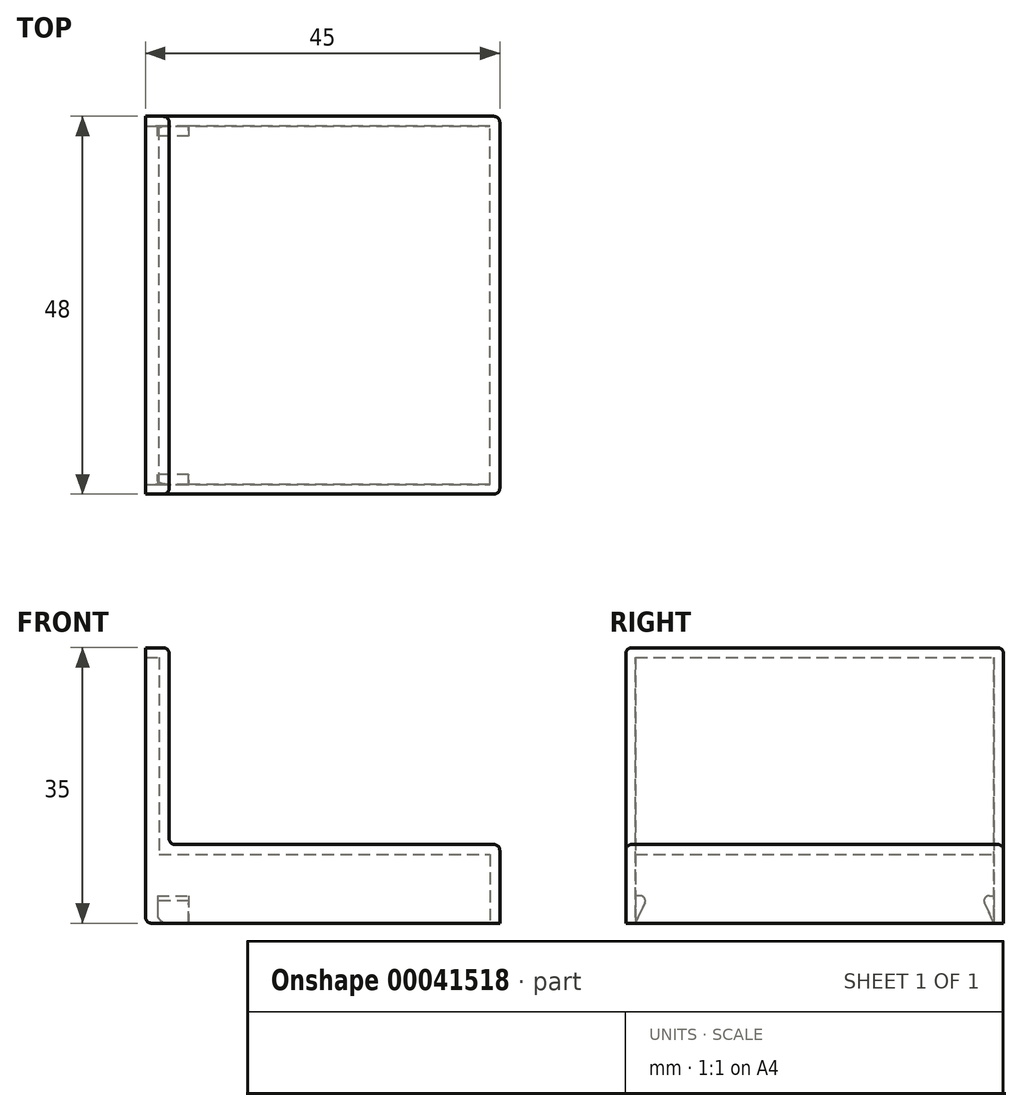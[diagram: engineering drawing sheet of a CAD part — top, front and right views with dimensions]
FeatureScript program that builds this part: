
annotation { "Feature Type Name" : "Feature", "Feature Type Description" : "" }
export const myFeature = defineFeature(function(context is Context, id is Id, definition is map)
    precondition{}
    {
        {
            var Q0;
            Q0=qCreatedBy(makeId("Front.planeOp"),FACE);
            var sketch = newSketch(context, id + "F0", { "sketchPlane" : qUnion([Q0])});
            skLineSegment(sketch, "E0", {"start": v(-44.9, -20.02) * mm, "end": v(-44.9, 14.98) * mm});
            skLineSegment(sketch, "E1", {"start": v(-44.9, 14.98) * mm, "end": v(-41.9, 14.98) * mm});
            skLineSegment(sketch, "E2", {"start": v(-41.9, 14.98) * mm, "end": v(-41.9, -10.02) * mm});
            skLineSegment(sketch, "E3", {"start": v(-41.9, -10.02) * mm, "end": v(0.1, -10.02) * mm});
            skLineSegment(sketch, "E4", {"start": v(0.1, -10.02) * mm, "end": v(0.1, -20.02) * mm});
            skLineSegment(sketch, "E5", {"start": v(0.1, -20.02) * mm, "end": v(-44.9, -20.02) * mm});
            skSolve(sketch);
        }
        {
            var Q0;
            Q0=makeQuery(id+"F0.imprint","IMPRINT",FACE,{"disambiguationData":[TD([[makeQuery(id+"F0.imprint","IMPRINT",EDGE,{"derivedFrom":sQuery(id+"F0.wireOp",EDGE,"E0")}),-1.0]])]});
            extrude(context, id + "F1", {"entities" : qUnion([Q0]), "depth" : 48 * mm});
        }
        {
            var Q0;
            Q0=makeQuery(id+"F1.opExtrude","SWEPT_FACE",FACE,{"disambiguationData":[OSD([sQuery(id+"F0.wireOp",EDGE,"E0")])]});
            var Q1;
            Q1=makeQuery(id+"F1.opExtrude","SWEPT_FACE",FACE,{"disambiguationData":[OSD([sQuery(id+"F0.wireOp",EDGE,"E5")])]});
            shell(context, id + "F2", {"entities" : qUnion([Q0, Q1]), "thickness" : 1.25 * mm});
        }
        {
            var Q0;
            Q0=makeQuery(id+"F1.opExtrude","CAP_EDGE",EDGE,{"disambiguationData":[OSD([sQuery(id+"F0.wireOp",EDGE,"E4")])],"isStart":false});
            var Q1;
            Q1=makeQuery(id+"F1.opExtrude","SWEPT_EDGE",EDGE,{"disambiguationData":[OSD([sQuery(id+"F0.wireOp",EDGE,"E3"),sQuery(id+"F0.wireOp",EDGE,"E4")])]});
            var Q2;
            Q2=makeQuery(id+"F1.opExtrude","CAP_EDGE",EDGE,{"disambiguationData":[OSD([sQuery(id+"F0.wireOp",EDGE,"E4")])],"isStart":true});
            var Q3;
            Q3=makeQuery(id+"F1.opExtrude","CAP_EDGE",EDGE,{"disambiguationData":[OSD([sQuery(id+"F0.wireOp",EDGE,"E3")])],"isStart":true});
            var Q4;
            Q4=makeQuery(id+"F1.opExtrude","SWEPT_FACE",FACE,{"disambiguationData":[OSD([sQuery(id+"F0.wireOp",EDGE,"E3")])]});
            var Q5;
            Q5=makeQuery(id+"F1.opExtrude","SWEPT_FACE",FACE,{"disambiguationData":[OSD([sQuery(id+"F0.wireOp",EDGE,"E2")])]});
            var Q6;
            Q6=makeQuery(id+"F1.opExtrude","CAP_EDGE",EDGE,{"disambiguationData":[OSD([sQuery(id+"F0.wireOp",EDGE,"E3")])],"isStart":false});
            var Q7;
            Q7=makeQuery(id+"F1.opExtrude","CAP_EDGE",EDGE,{"disambiguationData":[OSD([sQuery(id+"F0.wireOp",EDGE,"E2")])],"isStart":false});
            var Q8;
            Q8=makeQuery(id+"F1.opExtrude","CAP_EDGE",EDGE,{"disambiguationData":[OSD([sQuery(id+"F0.wireOp",EDGE,"E1")])],"isStart":false});
            var Q9;
            Q9=makeQuery(id+"F1.opExtrude","CAP_EDGE",EDGE,{"disambiguationData":[OSD([sQuery(id+"F0.wireOp",EDGE,"E1")])],"isStart":true});
            var Q10;
            Q10=makeQuery(id+"F1.opExtrude","SWEPT_EDGE",EDGE,{"disambiguationData":[OSD([sQuery(id+"F0.wireOp",EDGE,"E0"),sQuery(id+"F0.wireOp",EDGE,"E5")])]});
            var Q11;
            Q11=makeQuery(id+"F2.opShell","OFFSET_EDGE",EDGE,{"disambiguationData":[OSD([sQuery(id+"F0.wireOp",EDGE,"E0"),sQuery(id+"F0.wireOp",EDGE,"E5")])]});
            fillet(context, id + "F3", {"entities" : qUnion([Q0, Q1, Q2, Q3, Q4, Q5, Q6, Q7, Q8, Q9, Q10, Q11]), "radius" : 0.75 * mm, "tangentPropagation" : true, "allowEdgeOverflow" : false});
        }
        {
            var Q0;
            {var subQ0=sQuery(id+"F0.wireOp",EDGE,"E0");var subQ1=sQuery(id+"F0.wireOp",EDGE,"E1");var subQ2=sQuery(id+"F0.wireOp",EDGE,"E2");var subQ3=sQuery(id+"F0.wireOp",EDGE,"E3");var subQ4=sQuery(id+"F0.wireOp",EDGE,"E4");var subQ5=sQuery(id+"F0.wireOp",EDGE,"E5");Q0=makeQuery(id+"F2.opShell","OFFSET_FACE",FACE,{"disambiguationData":[OSD([subQ0,subQ1,subQ2,subQ3,subQ4,subQ5]),TDD([makeQuery(id+"F1.opExtrude","CAP_FACE",FACE,{"disambiguationData":[OSD([subQ0,subQ1,subQ2,subQ3,subQ4,subQ5])],"isStart":true})])]});}
            var sketch = newSketch(context, id + "F4", { "sketchPlane" : qUnion([Q0])});
            skLineSegment(sketch, "E6.bottom", {"start": v(-43.4, -16.52) * mm, "end": v(-39.4, -16.52) * mm});
            skLineSegment(sketch, "E6.top", {"start": v(-43.4, -20.02) * mm, "end": v(-39.4, -20.02) * mm});
            skLineSegment(sketch, "E6.left", {"start": v(-43.4, -16.52) * mm, "end": v(-43.4, -20.02) * mm});
            skLineSegment(sketch, "E6.right", {"start": v(-39.4, -16.52) * mm, "end": v(-39.4, -20.02) * mm});
            skSolve(sketch);
        }
        {
            var Q0;
            Q0 = qSketchRegion(id + "F4", true);
            extrude(context, id + "F5", {"entities" : qUnion([Q0]), "operationType" : NewBodyOperationType.ADD, "depth" : 1.25 * mm});
        }
        {
            var Q0;
            Q0=makeQuery(id+"F5.opExtrude","SWEPT_EDGE",EDGE,{"disambiguationData":[OSD([sQuery(id+"F0.wireOp",EDGE,"E5"),sQuery(id+"F4.wireOp",EDGE,"E6.top"),sQuery(id+"F4.wireOp",EDGE,"E6.left")])]});
            fillet(context, id + "F6", {"entities" : qUnion([Q0]), "radius" : 1.25 * mm, "tangentPropagation" : true, "allowEdgeOverflow" : false});
        }
        {
            var Q0;
            Q0=makeQuery(id+"F5.opExtrude","CAP_EDGE",EDGE,{"disambiguationData":[OSD([sQuery(id+"F4.wireOp",EDGE,"E6.top")])],"isStart":false});
            chamfer(context, id + "F7", {"entities" : qUnion([Q0]), "chamferType" : ChamferType.TWO_OFFSETS, "width1" : 1.25 * mm, "oppositeDirection" : false, "width2" : 2.75 * mm});
        }
        {
            var Q0;
            {var subQ0=sQuery(id+"F4.wireOp",EDGE,"E6.top");Q0=makeQuery(id+"F7.opChamfer","BLEND_EDGE",EDGE,{"blendedFrom":[makeQuery(id+"F5.opExtrude","CAP_EDGE",EDGE,{"disambiguationData":[OSD([subQ0])],"isStart":false}),makeQuery(id+"F5.opExtrude","CAP_FACE",FACE,{"disambiguationData":[OSD([sQuery(id+"F4.wireOp",EDGE,"E6.bottom"),subQ0,sQuery(id+"F4.wireOp",EDGE,"E6.left"),sQuery(id+"F4.wireOp",EDGE,"E6.right")])],"isStart":false})],"blendedInto":[makeQuery(id+"F5.opExtrude","CAP_FACE",FACE,{"disambiguationData":[OSD([sQuery(id+"F4.wireOp",EDGE,"E6.bottom"),subQ0,sQuery(id+"F4.wireOp",EDGE,"E6.left"),sQuery(id+"F4.wireOp",EDGE,"E6.right")])],"isStart":false})]});}
            var Q1;
            Q1=makeQuery(id+"F5.opExtrude","CAP_EDGE",EDGE,{"disambiguationData":[OSD([sQuery(id+"F4.wireOp",EDGE,"E6.bottom")])],"isStart":false});
            fillet(context, id + "F8", {"entities" : qUnion([Q0, Q1]), "radius" : 0.7 * mm, "tangentPropagation" : true, "allowEdgeOverflow" : false});
        }
        {
            var Q0;
            Q0=makeQuery(id+"F1.opExtrude","SWEPT_BODY",BODY,{"disambiguationData":[OSD([sQuery(id+"F0.wireOp",EDGE,"E0"),sQuery(id+"F0.wireOp",EDGE,"E1"),sQuery(id+"F0.wireOp",EDGE,"E2"),sQuery(id+"F0.wireOp",EDGE,"E3"),sQuery(id+"F0.wireOp",EDGE,"E4"),sQuery(id+"F0.wireOp",EDGE,"E5")])]});
            transform(context, id + "F9", {"entities" : qUnion([Q0]), "transformType" : TransformType.TRANSLATION_3D, "dx" : 0 * mm, "dy" : 24 * mm, "dz" : 0 * mm, "makeCopy" : false});
        }
        {
            var Q0;
            Q0=makeQuery(id+"F1.opExtrude","SWEPT_BODY",BODY,{"disambiguationData":[OSD([sQuery(id+"F0.wireOp",EDGE,"E0"),sQuery(id+"F0.wireOp",EDGE,"E1"),sQuery(id+"F0.wireOp",EDGE,"E2"),sQuery(id+"F0.wireOp",EDGE,"E3"),sQuery(id+"F0.wireOp",EDGE,"E4"),sQuery(id+"F0.wireOp",EDGE,"E5")])]});
            var Q1;
            Q1=qCreatedBy(makeId("Front.planeOp"),FACE);
            mirror(context, id + "F10", {"operationType" : NewBodyOperationType.ADD, "entities" : qUnion([Q0]), "mirrorPlane" : qUnion([Q1])});
        }
    });
